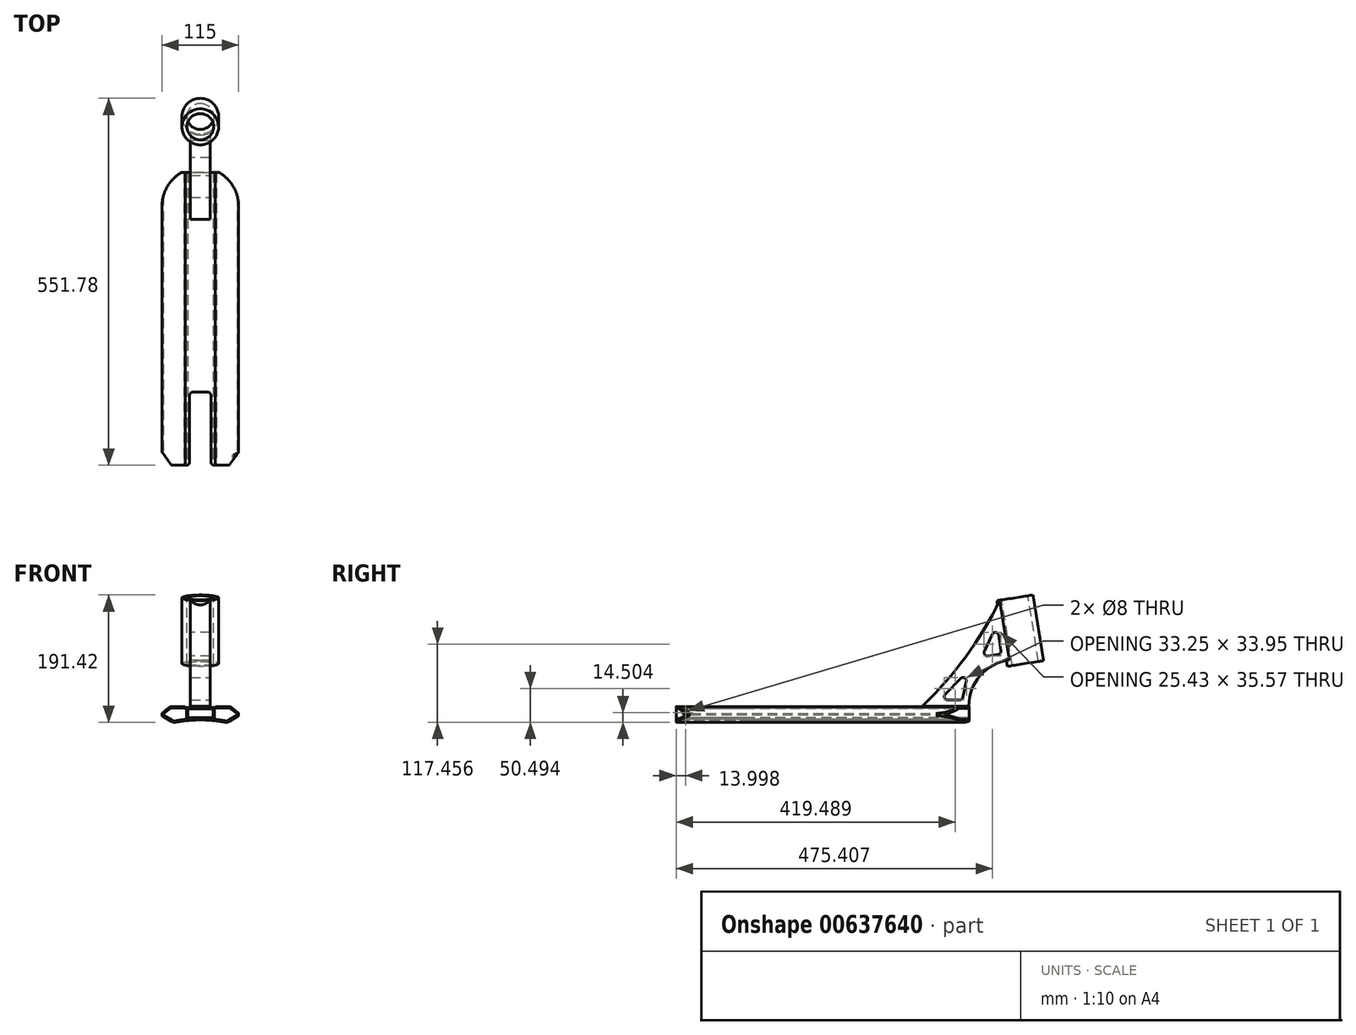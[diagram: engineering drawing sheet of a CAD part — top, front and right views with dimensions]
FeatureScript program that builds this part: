
annotation { "Feature Type Name" : "Feature", "Feature Type Description" : "" }
export const myFeature = defineFeature(function(context is Context, id is Id, definition is map)
    precondition{}
    {
        {
            var Q0;
            Q0=qCreatedBy(makeId("Front.planeOp"),FACE);
            var sketch = newSketch(context, id + "F0", { "sketchPlane" : qUnion([Q0])});
            skLineSegment(sketch, "E0", {"start": v(0, 0) * mm, "end": v(0, 46.3) * mm, "construction": true});
            skLineSegment(sketch, "E1", {"start": v(0, 23.15) * mm, "end": v(22.5, 23.15) * mm});
            skLineSegment(sketch, "E2", {"start": v(22.5, 23.15) * mm, "end": v(22.5, 24.45) * mm});
            skLineSegment(sketch, "E3", {"start": v(22.5, 24.45) * mm, "end": v(45.58, 24.45) * mm});
            skLineSegment(sketch, "E4", {"start": v(45.58, 24.45) * mm, "end": v(57.5, 14.45) * mm});
            skLineSegment(sketch, "E5", {"start": v(57.5, 14.45) * mm, "end": v(57.5, 10.45) * mm});
            skLineSegment(sketch, "E6", {"start": v(57.5, 10.45) * mm, "end": v(40.18, 0.45) * mm});
            skLineSegment(sketch, "E7.MirrorCS", {"start": v(0, 23.15) * mm, "end": v(-22.5, 23.15) * mm});
            skLineSegment(sketch, "E8.MirrorCS", {"start": v(-22.5, 24.45) * mm, "end": v(-45.58, 24.45) * mm});
            skLineSegment(sketch, "E9.MirrorCS", {"start": v(-45.58, 24.45) * mm, "end": v(-57.5, 14.45) * mm});
            skLineSegment(sketch, "E10.MirrorCS", {"start": v(-22.5, 23.15) * mm, "end": v(-22.5, 24.45) * mm});
            skLineSegment(sketch, "E11.MirrorCS", {"start": v(-57.5, 14.45) * mm, "end": v(-57.5, 10.45) * mm});
            skLineSegment(sketch, "E12.MirrorCS", {"start": v(-57.5, 10.45) * mm, "end": v(-40.18, 0.45) * mm});
            skArc(sketch, "E13", {"start": v(40.18, 0.45) * mm, "mid": v(0, 4.53) * mm, "end": v(-40.18, 0.45) * mm});
            skSolve(sketch);
        }
        {
            var Q0;
            Q0 = qSketchRegion(id + "F0", true);
            extrude(context, id + "F1", {"entities" : qUnion([Q0]), "endBound" : BoundingType.SYMMETRIC, "depth" : 500 * mm, "offsetDistance" : 25 * mm});
        }
        {
            var Q0;
            Q0=qCreatedBy(makeId("Front.planeOp"),FACE);
            var sketch = newSketch(context, id + "F2", { "sketchPlane" : qUnion([Q0])});
            skLineSegment(sketch, "E14.bottom", {"start": v(-19, 21.15) * mm, "end": v(19, 21.15) * mm});
            skLineSegment(sketch, "E14.top", {"start": v(-19, 8.15) * mm, "end": v(19, 8.15) * mm});
            skLineSegment(sketch, "E14.left", {"start": v(-19, 21.15) * mm, "end": v(-19, 8.15) * mm});
            skLineSegment(sketch, "E14.right", {"start": v(19, 21.15) * mm, "end": v(19, 8.15) * mm});
            skSolve(sketch);
        }
        {
            var Q0;
            Q0 = qSketchRegion(id + "F2", true);
            extrude(context, id + "F3", {"entities" : qUnion([Q0]), "operationType" : NewBodyOperationType.REMOVE, "endBound" : BoundingType.SYMMETRIC, "oppositeDirection" : true, "depth" : 500 * mm, "offsetDistance" : 25 * mm});
        }
        {
            var Q0;
            Q0=makeQuery(id+"F1.opExtrude","SWEPT_EDGE",EDGE,{"disambiguationData":[OSD([sQuery(id+"F0.wireOp",EDGE,"E8.MirrorCS"),sQuery(id+"F0.wireOp",EDGE,"E10.MirrorCS")])]});
            var Q1;
            Q1=makeQuery(id+"F1.opExtrude","SWEPT_EDGE",EDGE,{"disambiguationData":[OSD([sQuery(id+"F0.wireOp",EDGE,"E2"),sQuery(id+"F0.wireOp",EDGE,"E3")])]});
            fillet(context, id + "F4", {"entities" : qUnion([Q0, Q1]), "radius" : 2 * mm, "tangentPropagation" : true, "allowEdgeOverflow" : false});
        }
        {
            var Q0;
            Q0=makeQuery(id+"F1.opExtrude","SWEPT_EDGE",EDGE,{"disambiguationData":[OSD([sQuery(id+"F0.wireOp",EDGE,"E3"),sQuery(id+"F0.wireOp",EDGE,"E4")])]});
            var Q1;
            Q1=makeQuery(id+"F1.opExtrude","SWEPT_EDGE",EDGE,{"disambiguationData":[OSD([sQuery(id+"F0.wireOp",EDGE,"E6"),sQuery(id+"F0.wireOp",EDGE,"E13")])]});
            var Q2;
            Q2=makeQuery(id+"F1.opExtrude","SWEPT_EDGE",EDGE,{"disambiguationData":[OSD([sQuery(id+"F0.wireOp",EDGE,"E8.MirrorCS"),sQuery(id+"F0.wireOp",EDGE,"E9.MirrorCS")])]});
            var Q3;
            Q3=makeQuery(id+"F1.opExtrude","SWEPT_EDGE",EDGE,{"disambiguationData":[OSD([sQuery(id+"F0.wireOp",EDGE,"E12.MirrorCS"),sQuery(id+"F0.wireOp",EDGE,"E13")])]});
            fillet(context, id + "F5", {"entities" : qUnion([Q0, Q1, Q2, Q3]), "radius" : 9 * mm, "tangentPropagation" : true, "allowEdgeOverflow" : false});
        }
        {
            var Q0;
            Q0=makeQuery(id+"F1.opExtrude","SWEPT_EDGE",EDGE,{"disambiguationData":[OSD([sQuery(id+"F0.wireOp",EDGE,"E4"),sQuery(id+"F0.wireOp",EDGE,"E5")])]});
            var Q1;
            Q1=makeQuery(id+"F1.opExtrude","SWEPT_EDGE",EDGE,{"disambiguationData":[OSD([sQuery(id+"F0.wireOp",EDGE,"E5"),sQuery(id+"F0.wireOp",EDGE,"E6")])]});
            var Q2;
            Q2=makeQuery(id+"F1.opExtrude","SWEPT_EDGE",EDGE,{"disambiguationData":[OSD([sQuery(id+"F0.wireOp",EDGE,"E9.MirrorCS"),sQuery(id+"F0.wireOp",EDGE,"E11.MirrorCS")])]});
            var Q3;
            Q3=makeQuery(id+"F1.opExtrude","SWEPT_EDGE",EDGE,{"disambiguationData":[OSD([sQuery(id+"F0.wireOp",EDGE,"E11.MirrorCS"),sQuery(id+"F0.wireOp",EDGE,"E12.MirrorCS")])]});
            fillet(context, id + "F6", {"entities" : qUnion([Q0, Q1, Q2, Q3]), "radius" : 1 * mm, "tangentPropagation" : true, "allowEdgeOverflow" : false});
        }
        {
            var Q0;
            Q0=makeQuery(id+"F1.opExtrude","CAP_FACE",FACE,{"disambiguationData":[OSD([sQuery(id+"F0.wireOp",EDGE,"E1"),sQuery(id+"F0.wireOp",EDGE,"E2"),sQuery(id+"F0.wireOp",EDGE,"E3"),sQuery(id+"F0.wireOp",EDGE,"E4"),sQuery(id+"F0.wireOp",EDGE,"E5"),sQuery(id+"F0.wireOp",EDGE,"E6"),sQuery(id+"F0.wireOp",EDGE,"E7.MirrorCS"),sQuery(id+"F0.wireOp",EDGE,"E8.MirrorCS"),sQuery(id+"F0.wireOp",EDGE,"E9.MirrorCS"),sQuery(id+"F0.wireOp",EDGE,"E10.MirrorCS"),sQuery(id+"F0.wireOp",EDGE,"E11.MirrorCS"),sQuery(id+"F0.wireOp",EDGE,"E12.MirrorCS"),sQuery(id+"F0.wireOp",EDGE,"E13")])],"isStart":false});
            var sketch = newSketch(context, id + "F7", { "sketchPlane" : qUnion([Q0])});
            skLineSegment(sketch, "E15.0.0", {"start": v(-57.5, 13.98) * mm, "end": v(-57.5, 11.03) * mm});
            skArc(sketch, "E15.0.1", {"start": v(-57.5, 11.03) * mm, "mid": v(-57.37, 10.53) * mm, "end": v(-57, 10.16) * mm});
            skLineSegment(sketch, "E15.0.2", {"start": v(-57, 10.16) * mm, "end": v(-43.1, 2.14) * mm});
            skArc(sketch, "E15.0.3", {"start": v(-43.1, 2.14) * mm, "mid": v(-40.12, 1.06) * mm, "end": v(-36.94, 1.09) * mm});
            skArc(sketch, "E15.0.4", {"start": v(-36.94, 1.09) * mm, "mid": v(0, 4.53) * mm, "end": v(36.94, 1.09) * mm});
            skArc(sketch, "E15.0.5", {"start": v(36.94, 1.09) * mm, "mid": v(40.12, 1.06) * mm, "end": v(43.1, 2.14) * mm});
            skLineSegment(sketch, "E15.0.6", {"start": v(43.1, 2.14) * mm, "end": v(57, 10.16) * mm});
            skArc(sketch, "E15.0.7", {"start": v(57, 10.16) * mm, "mid": v(57.37, 10.53) * mm, "end": v(57.5, 11.03) * mm});
            skLineSegment(sketch, "E15.0.8", {"start": v(57.5, 11.03) * mm, "end": v(57.5, 13.98) * mm});
            skArc(sketch, "E15.0.9", {"start": v(57.5, 13.98) * mm, "mid": v(57.4, 14.4) * mm, "end": v(57.14, 14.75) * mm});
            skLineSegment(sketch, "E15.0.10", {"start": v(57.14, 14.75) * mm, "end": v(48.1, 22.35) * mm});
            skArc(sketch, "E15.0.11", {"start": v(48.1, 22.35) * mm, "mid": v(45.38, 23.9) * mm, "end": v(42.3, 24.45) * mm});
            skLineSegment(sketch, "E15.0.12", {"start": v(42.3, 24.45) * mm, "end": v(24.37, 24.45) * mm});
            skArc(sketch, "E15.0.13", {"start": v(24.37, 24.45) * mm, "mid": v(23.23, 24.1) * mm, "end": v(22.5, 23.15) * mm});
            skLineSegment(sketch, "E15.0.14", {"start": v(22.5, 23.15) * mm, "end": v(-22.5, 23.15) * mm});
            skArc(sketch, "E15.0.15", {"start": v(-22.5, 23.15) * mm, "mid": v(-23.23, 24.1) * mm, "end": v(-24.37, 24.45) * mm});
            skLineSegment(sketch, "E15.0.16", {"start": v(-24.37, 24.45) * mm, "end": v(-42.3, 24.45) * mm});
            skArc(sketch, "E15.0.17", {"start": v(-42.3, 24.45) * mm, "mid": v(-45.38, 23.9) * mm, "end": v(-48.1, 22.35) * mm});
            skLineSegment(sketch, "E15.0.18", {"start": v(-48.1, 22.35) * mm, "end": v(-57.14, 14.75) * mm});
            skArc(sketch, "E15.0.19", {"start": v(-57.14, 14.75) * mm, "mid": v(-57.4, 14.4) * mm, "end": v(-57.5, 13.98) * mm});
            skArc(sketch, "E16.0", {"start": v(-37.3, 3.05) * mm, "mid": v(0, 6.53) * mm, "end": v(37.3, 3.05) * mm});
            skArc(sketch, "E16.1", {"start": v(-42.1, 3.87) * mm, "mid": v(-39.78, 3.03) * mm, "end": v(-37.3, 3.05) * mm});
            skLineSegment(sketch, "E16.2", {"start": v(-55.5, 11.6) * mm, "end": v(-42.1, 3.87) * mm});
            skLineSegment(sketch, "E16.3", {"start": v(-55.5, 13.52) * mm, "end": v(-55.5, 11.6) * mm});
            skLineSegment(sketch, "E16.4", {"start": v(-24.37, 22.45) * mm, "end": v(-24.37, 22.45) * mm});
            skLineSegment(sketch, "E16.5", {"start": v(-24.37, 22.45) * mm, "end": v(-42.3, 22.45) * mm});
            skArc(sketch, "E16.6", {"start": v(-42.3, 22.45) * mm, "mid": v(-44.7, 22.03) * mm, "end": v(-46.8, 20.81) * mm});
            skLineSegment(sketch, "E16.7", {"start": v(-46.8, 20.81) * mm, "end": v(-55.5, 13.52) * mm});
            skArc(sketch, "E17", {"start": v(-22.73, 21.88) * mm, "mid": v(-23.48, 22.35) * mm, "end": v(-24.37, 22.45) * mm});
            skLineSegment(sketch, "E18", {"start": v(-22.73, 21.88) * mm, "end": v(-21, 21.88) * mm});
            skLineSegment(sketch, "E19", {"start": v(-21, 21.88) * mm, "end": v(-21, 5.43) * mm});
            skLineSegment(sketch, "E20.MirrorCS", {"start": v(21, 21.88) * mm, "end": v(21, 5.43) * mm});
            skLineSegment(sketch, "E21.MirrorCS", {"start": v(22.73, 21.88) * mm, "end": v(21, 21.88) * mm});
            skArc(sketch, "E22.MirrorCS", {"start": v(22.73, 21.88) * mm, "mid": v(23.48, 22.35) * mm, "end": v(24.37, 22.45) * mm});
            skLineSegment(sketch, "E23.MirrorCS", {"start": v(24.37, 22.45) * mm, "end": v(42.3, 22.45) * mm});
            skArc(sketch, "E24.MirrorCS", {"start": v(42.3, 22.45) * mm, "mid": v(44.7, 22.03) * mm, "end": v(46.8, 20.81) * mm});
            skLineSegment(sketch, "E25.MirrorCS", {"start": v(46.8, 20.81) * mm, "end": v(55.5, 13.52) * mm});
            skLineSegment(sketch, "E26.MirrorCS", {"start": v(55.5, 13.52) * mm, "end": v(55.5, 11.6) * mm});
            skLineSegment(sketch, "E27.MirrorCS", {"start": v(55.5, 11.6) * mm, "end": v(42.1, 3.87) * mm});
            skArc(sketch, "E28.MirrorCS", {"start": v(42.1, 3.87) * mm, "mid": v(39.78, 3.03) * mm, "end": v(37.3, 3.05) * mm});
            skArc(sketch, "E29.MirrorCS", {"start": v(37.3, 3.05) * mm, "mid": v(0, 6.53) * mm, "end": v(-37.3, 3.05) * mm});
            skSolve(sketch);
        }
        {
            var Q0;
            {var subQ0=sQuery(id+"F7.wireOp",EDGE,"E16.1");Q0=makeQuery(id+"F7.imprint","IMPRINT",FACE,{"disambiguationData":[TD([[makeQuery(id+"F7.imprint","IMPRINT",EDGE,{"derivedFrom":subQ0}),1.0]])]});}
            var Q1;
            Q1=makeQuery(id+"F7.imprint","IMPRINT",FACE,{"disambiguationData":[TD([[makeQuery(id+"F7.imprint","IMPRINT",EDGE,{"derivedFrom":sQuery(id+"F7.wireOp",EDGE,"E21.MirrorCS")}),1.0]])]});
            extrude(context, id + "F8", {"entities" : qUnion([Q0, Q1]), "operationType" : NewBodyOperationType.REMOVE, "endBound" : BoundingType.THROUGH_ALL, "oppositeDirection" : true, "depth" : 25 * mm, "offsetDistance" : 25 * mm});
        }
        {
            var Q0;
            Q0=qCreatedBy(makeId("Top.planeOp"),FACE);
            var sketch = newSketch(context, id + "F9", { "sketchPlane" : qUnion([Q0])});
            skArc(sketch, "E30", {"start": v(57.5, 199.99) * mm, "mid": v(0.07, 257.5) * mm, "end": v(-57.5, 200.13) * mm});
            skLineSegment(sketch, "E31.bottom", {"start": v(57.51, 199.99) * mm, "end": v(-57.5, 199.99) * mm});
            skLineSegment(sketch, "E31.top", {"start": v(57.51, 279.99) * mm, "end": v(-57.5, 279.99) * mm});
            skLineSegment(sketch, "E31.left", {"start": v(57.51, 199.99) * mm, "end": v(57.51, 279.99) * mm});
            skLineSegment(sketch, "E31.right", {"start": v(-57.5, 199.99) * mm, "end": v(-57.5, 279.99) * mm});
            skSolve(sketch);
        }
        {
            var Q0;
            {var subQ3=sQuery(id+"F9.wireOp",EDGE,"E30");Q0=makeQuery(id+"F9.imprint","IMPRINT",FACE,{"disambiguationData":[TD([[makeQuery(id+"F9.imprint","IMPRINT",EDGE,{"derivedFrom":subQ3}),-1.0]])]});}
            extrude(context, id + "F10", {"entities" : qUnion([Q0]), "operationType" : NewBodyOperationType.REMOVE, "endBound" : BoundingType.THROUGH_ALL, "depth" : 25 * mm, "offsetDistance" : 25 * mm});
        }
        {
            var Q0;
            {var subQ3=sQuery(id+"F9.wireOp",EDGE,"E30");Q0=makeQuery(id+"F9.imprint","IMPRINT",FACE,{"disambiguationData":[TD([[makeQuery(id+"F9.imprint","IMPRINT",EDGE,{"derivedFrom":subQ3}),-1.0]])]});}
            extrude(context, id + "F11", {"entities" : qUnion([Q0]), "operationType" : NewBodyOperationType.REMOVE, "endBound" : BoundingType.THROUGH_ALL, "oppositeDirection" : true, "depth" : 25 * mm, "offsetDistance" : 25 * mm, "hasSecondDirection" : true, "secondDirectionOppositeDirection" : false, "secondDirectionDepth" : 25 * mm});
        }
        {
            var Q0;
            Q0=qCreatedBy(makeId("Top.planeOp"),FACE);
            var sketch = newSketch(context, id + "F12", { "sketchPlane" : qUnion([Q0])});
            skLineSegment(sketch, "E32", {"start": v(-68, -156.01) * mm, "end": v(-68, -286.01) * mm});
            skLineSegment(sketch, "E33", {"start": v(-68, -286.01) * mm, "end": v(68, -286.01) * mm});
            skLineSegment(sketch, "E34", {"start": v(68, -286.01) * mm, "end": v(68, -156.01) * mm});
            skLineSegment(sketch, "E35", {"start": v(68, -156.01) * mm, "end": v(43.3, -190.01) * mm});
            skLineSegment(sketch, "E36", {"start": v(43.3, -190.01) * mm, "end": v(16, -190.01) * mm});
            skLineSegment(sketch, "E37", {"start": v(16, -190.01) * mm, "end": v(16, -80.01) * mm});
            skLineSegment(sketch, "E38", {"start": v(16, -80.01) * mm, "end": v(-16, -80.01) * mm});
            skLineSegment(sketch, "E39", {"start": v(-16, -80.01) * mm, "end": v(-16, -190.01) * mm});
            skLineSegment(sketch, "E40", {"start": v(-16, -190.01) * mm, "end": v(-43.3, -190.01) * mm});
            skLineSegment(sketch, "E41", {"start": v(-43.3, -190.01) * mm, "end": v(-68, -156.01) * mm});
            skSolve(sketch);
        }
        {
            var Q0;
            Q0 = qSketchRegion(id + "F12", true);
            extrude(context, id + "F13", {"entities" : qUnion([Q0]), "operationType" : NewBodyOperationType.REMOVE, "endBound" : BoundingType.THROUGH_ALL, "oppositeDirection" : true, "depth" : 25 * mm, "offsetDistance" : 25 * mm, "hasSecondDirection" : true, "secondDirectionBound" : SecondDirectionBoundingType.THROUGH_ALL, "secondDirectionOppositeDirection" : false, "secondDirectionDepth" : 25 * mm});
        }
        {
            var Q0;
            {var subQ0=sQuery(id+"F12.wireOp",EDGE,"E38");var subQ1=sQuery(id+"F12.wireOp",EDGE,"E39");Q0=makeQuery(id+"F13.boolean.opBoolean","COPY",EDGE,{"disambiguationData":[TD([makeQuery(id+"F3.boolean.opBoolean","COPY",FACE,{"derivedFrom":makeQuery(id+"F3.opExtrude","SWEPT_FACE",FACE,{"disambiguationData":[OSD([sQuery(id+"F2.wireOp",EDGE,"E14.bottom")])]})})])],"derivedFrom":makeQuery(id+"F13.opExtrude","SWEPT_EDGE",EDGE,{"disambiguationData":[OSD([subQ0,subQ1])]})});}
            var Q1;
            {var subQ0=sQuery(id+"F12.wireOp",EDGE,"E37");var subQ1=sQuery(id+"F12.wireOp",EDGE,"E38");Q1=makeQuery(id+"F13.boolean.opBoolean","COPY",EDGE,{"disambiguationData":[TD([makeQuery(id+"F3.boolean.opBoolean","COPY",FACE,{"derivedFrom":makeQuery(id+"F3.opExtrude","SWEPT_FACE",FACE,{"disambiguationData":[OSD([sQuery(id+"F2.wireOp",EDGE,"E14.bottom")])]})})])],"derivedFrom":makeQuery(id+"F13.opExtrude","SWEPT_EDGE",EDGE,{"disambiguationData":[OSD([subQ0,subQ1])]})});}
            var Q2;
            {var subQ0=sQuery(id+"F12.wireOp",EDGE,"E38");var subQ1=sQuery(id+"F12.wireOp",EDGE,"E37");Q2=makeQuery(id+"F13.boolean.opBoolean","COPY",EDGE,{"disambiguationData":[TD([makeQuery(id+"F1.opExtrude","SWEPT_FACE",FACE,{"disambiguationData":[OSD([sQuery(id+"F0.wireOp",EDGE,"E13")])]})])],"derivedFrom":makeQuery(id+"F13.opExtrude","SWEPT_EDGE",EDGE,{"disambiguationData":[OSD([subQ1,subQ0])]})});}
            var Q3;
            {var subQ0=sQuery(id+"F12.wireOp",EDGE,"E38");var subQ1=sQuery(id+"F12.wireOp",EDGE,"E39");Q3=makeQuery(id+"F13.boolean.opBoolean","COPY",EDGE,{"disambiguationData":[TD([makeQuery(id+"F1.opExtrude","SWEPT_FACE",FACE,{"disambiguationData":[OSD([sQuery(id+"F0.wireOp",EDGE,"E13")])]})])],"derivedFrom":makeQuery(id+"F13.opExtrude","SWEPT_EDGE",EDGE,{"disambiguationData":[OSD([subQ0,subQ1])]})});}
            var Q4;
            {var subQ0=sQuery(id+"F12.wireOp",EDGE,"E40");var subQ1=sQuery(id+"F12.wireOp",EDGE,"E39");Q4=makeQuery(id+"F13.boolean.opBoolean","COPY",EDGE,{"disambiguationData":[TD([makeQuery(id+"F3.boolean.opBoolean","COPY",FACE,{"derivedFrom":makeQuery(id+"F3.opExtrude","SWEPT_FACE",FACE,{"disambiguationData":[OSD([sQuery(id+"F2.wireOp",EDGE,"E14.bottom")])]})})])],"derivedFrom":makeQuery(id+"F13.opExtrude","SWEPT_EDGE",EDGE,{"disambiguationData":[OSD([subQ1,subQ0])]})});}
            var Q5;
            {var subQ0=sQuery(id+"F12.wireOp",EDGE,"E37");var subQ1=sQuery(id+"F12.wireOp",EDGE,"E36");Q5=makeQuery(id+"F13.boolean.opBoolean","COPY",EDGE,{"disambiguationData":[TD([makeQuery(id+"F3.boolean.opBoolean","COPY",FACE,{"derivedFrom":makeQuery(id+"F3.opExtrude","SWEPT_FACE",FACE,{"disambiguationData":[OSD([sQuery(id+"F2.wireOp",EDGE,"E14.bottom")])]})})])],"derivedFrom":makeQuery(id+"F13.opExtrude","SWEPT_EDGE",EDGE,{"disambiguationData":[OSD([subQ1,subQ0])]})});}
            var Q6;
            {var subQ0=sQuery(id+"F12.wireOp",EDGE,"E39");var subQ1=sQuery(id+"F12.wireOp",EDGE,"E40");Q6=makeQuery(id+"F13.boolean.opBoolean","COPY",EDGE,{"disambiguationData":[TD([makeQuery(id+"F1.opExtrude","SWEPT_FACE",FACE,{"disambiguationData":[OSD([sQuery(id+"F0.wireOp",EDGE,"E13")])]})])],"derivedFrom":makeQuery(id+"F13.opExtrude","SWEPT_EDGE",EDGE,{"disambiguationData":[OSD([subQ0,subQ1])]})});}
            var Q7;
            {var subQ0=sQuery(id+"F12.wireOp",EDGE,"E36");var subQ1=sQuery(id+"F12.wireOp",EDGE,"E37");Q7=makeQuery(id+"F13.boolean.opBoolean","COPY",EDGE,{"disambiguationData":[TD([makeQuery(id+"F1.opExtrude","SWEPT_FACE",FACE,{"disambiguationData":[OSD([sQuery(id+"F0.wireOp",EDGE,"E13")])]})])],"derivedFrom":makeQuery(id+"F13.opExtrude","SWEPT_EDGE",EDGE,{"disambiguationData":[OSD([subQ0,subQ1])]})});}
            fillet(context, id + "F14", {"entities" : qUnion([Q0, Q1, Q2, Q3, Q4, Q5, Q6, Q7]), "radius" : 5 * mm, "tangentPropagation" : true, "allowEdgeOverflow" : false});
        }
        {
            var Q0;
            Q0=qCreatedBy(makeId("Right.planeOp"),FACE);
            var sketch = newSketch(context, id + "F15", { "sketchPlane" : qUnion([Q0])});
            skLineSegment(sketch, "E42", {"start": v(249.7, 25.24) * mm, "end": v(179.7, 25.24) * mm});
            skArc(sketch, "E43", {"start": v(179.7, 25.24) * mm, "mid": v(245.17, 99.57) * mm, "end": v(296.25, 184.45) * mm});
            skLineSegment(sketch, "E44", {"start": v(296.25, 184.45) * mm, "end": v(341.68, 191.65) * mm});
            skLineSegment(sketch, "E45", {"start": v(341.68, 191.65) * mm, "end": v(357.32, 92.88) * mm});
            skLineSegment(sketch, "E46", {"start": v(357.32, 92.88) * mm, "end": v(311.9, 85.68) * mm});
            skLineSegment(sketch, "E47", {"start": v(311.9, 85.68) * mm, "end": v(310.47, 94.63) * mm});
            skArc(sketch, "E48", {"start": v(310.47, 94.63) * mm, "mid": v(267.04, 71.36) * mm, "end": v(249.7, 25.24) * mm});
            skSolve(sketch);
        }
        {
            var Q0;
            Q0=makeQuery(id+"F15.imprint","IMPRINT",FACE,{"disambiguationData":[TD([[makeQuery(id+"F15.imprint","IMPRINT",EDGE,{"derivedFrom":sQuery(id+"F15.wireOp",EDGE,"E42")}),-1.0]])]});
            extrude(context, id + "F16", {"entities" : qUnion([Q0]), "operationType" : NewBodyOperationType.ADD, "endBound" : BoundingType.SYMMETRIC, "depth" : 30 * mm, "offsetDistance" : 25 * mm});
        }
        {
            var Q0;
            Q0=makeQuery(id+"F16.opExtrude","SWEPT_FACE",FACE,{"disambiguationData":[OSD([sQuery(id+"F15.wireOp",EDGE,"E44")])]});
            var sketch = newSketch(context, id + "F17", { "sketchPlane" : qUnion([Q0])});
            skCircle(sketch, "E49", {"center": v(0, 344.45) * mm, "radius": 27.5 * mm});
            skSolve(sketch);
        }
        {
            var Q0;
            Q0=makeQuery(id+"F17.imprint","IMPRINT",FACE,{"disambiguationData":[TD([[makeQuery(id+"F17.imprint","IMPRINT",EDGE,{"derivedFrom":sQuery(id+"F17.wireOp",EDGE,"E49")}),1.0]])]});
            var Q1;
            Q1=makeQuery(id+"F16.opExtrude","SWEPT_FACE",FACE,{"disambiguationData":[OSD([sQuery(id+"F15.wireOp",EDGE,"E46")])]});
            extrude(context, id + "F18", {"entities" : qUnion([Q0]), "operationType" : NewBodyOperationType.ADD, "endBound" : BoundingType.UP_TO_SURFACE, "oppositeDirection" : true, "depth" : 25 * mm, "endBoundEntityFace" : qUnion([Q1]), "offsetDistance" : 25 * mm});
        }
        {
            var Q0;
            {var subQ0=sQuery(id+"F15.wireOp",EDGE,"E44");Q0=makeQuery(id+"F18.boolean.opBoolean","MERGE",FACE,{"derivedFrom":[makeQuery(id+"F16.opExtrude","SWEPT_FACE",FACE,{"disambiguationData":[OSD([subQ0])]}),makeQuery(id+"F18.opExtrude","CAP_FACE",FACE,{"disambiguationData":[OSD([sQuery(id+"F15.wireOp",EDGE,"E43"),subQ0,sQuery(id+"F15.wireOp",EDGE,"E45"),sQuery(id+"F17.wireOp",EDGE,"E49")])],"isStart":true})]});}
            var sketch = newSketch(context, id + "F19", { "sketchPlane" : qUnion([Q0])});
            skPoint(sketch, "E50", {"position": v(0, 344.45) * mm});
            skSolve(sketch);
        }
        {
            var Q0;
            Q0=sQuery(id+"F19.wireOp",VERTEX,"E50");
            var Q1;
            Q1=makeQuery(id+"F16.opExtrude","SWEPT_BODY",BODY,{"disambiguationData":[OSD([sQuery(id+"F15.wireOp",EDGE,"E42"),sQuery(id+"F15.wireOp",EDGE,"E43"),sQuery(id+"F15.wireOp",EDGE,"E44"),sQuery(id+"F15.wireOp",EDGE,"E45"),sQuery(id+"F15.wireOp",EDGE,"E46"),sQuery(id+"F15.wireOp",EDGE,"E47"),sQuery(id+"F15.wireOp",EDGE,"E48")])]});
            hole(context, id + "F20", {"style" : HoleStyle.SIMPLE, "endStyle" : HoleEndStyle.THROUGH, "holeDiameter" : 40 * mm, "majorDiameter" : 5 * mm, "isTappedThrough" : true, "tappedDepth" : 12 * mm, "tapClearance" : 3, "locations" : qUnion([Q0]), "scope" : qUnion([Q1])});
        }
        {
            var Q0;
            Q0=makeQuery(id+"F8.boolean.opBoolean","COPY",FACE,{"derivedFrom":makeQuery(id+"F8.opExtrude","SWEPT_FACE",FACE,{"disambiguationData":[OSD([sQuery(id+"F7.wireOp",EDGE,"E19")])]})});
            var sketch = newSketch(context, id + "F21", { "sketchPlane" : qUnion([Q0])});
            skPoint(sketch, "E51", {"position": v(176.01, 15.43) * mm});
            skSolve(sketch);
        }
        {
            var Q0;
            Q0=sQuery(id+"F21.wireOp",VERTEX,"E51");
            var Q1;
            Q1=makeQuery(id+"F1.opExtrude","SWEPT_BODY",BODY,{"disambiguationData":[OSD([sQuery(id+"F0.wireOp",EDGE,"E1"),sQuery(id+"F0.wireOp",EDGE,"E2"),sQuery(id+"F0.wireOp",EDGE,"E3"),sQuery(id+"F0.wireOp",EDGE,"E4"),sQuery(id+"F0.wireOp",EDGE,"E5"),sQuery(id+"F0.wireOp",EDGE,"E6"),sQuery(id+"F0.wireOp",EDGE,"E7.MirrorCS"),sQuery(id+"F0.wireOp",EDGE,"E8.MirrorCS"),sQuery(id+"F0.wireOp",EDGE,"E9.MirrorCS"),sQuery(id+"F0.wireOp",EDGE,"E10.MirrorCS"),sQuery(id+"F0.wireOp",EDGE,"E11.MirrorCS"),sQuery(id+"F0.wireOp",EDGE,"E12.MirrorCS"),sQuery(id+"F0.wireOp",EDGE,"E13")])]});
            hole(context, id + "F22", {"style" : HoleStyle.SIMPLE, "endStyle" : HoleEndStyle.THROUGH, "holeDiameter" : 8 * mm, "majorDiameter" : 5 * mm, "isTappedThrough" : true, "tappedDepth" : 12 * mm, "tapClearance" : 3, "locations" : qUnion([Q0]), "scope" : qUnion([Q1])});
        }
        {
            var Q0;
            Q0=makeQuery(id+"F16.opExtrude","CAP_FACE",FACE,{"disambiguationData":[OSD([sQuery(id+"F15.wireOp",EDGE,"E42"),sQuery(id+"F15.wireOp",EDGE,"E43"),sQuery(id+"F15.wireOp",EDGE,"E44"),sQuery(id+"F15.wireOp",EDGE,"E45"),sQuery(id+"F15.wireOp",EDGE,"E46"),sQuery(id+"F15.wireOp",EDGE,"E47"),sQuery(id+"F15.wireOp",EDGE,"E48")])],"isStart":false});
            var sketch = newSketch(context, id + "F23", { "sketchPlane" : qUnion([Q0])});
            skLineSegment(sketch, "E52", {"start": v(206, 34.45) * mm, "end": v(240, 34.45) * mm});
            skLineSegment(sketch, "E53", {"start": v(240, 34.45) * mm, "end": v(249.7, 79.45) * mm});
            skLineSegment(sketch, "E54", {"start": v(206, 34.45) * mm, "end": v(249.7, 79.45) * mm});
            skLineSegment(sketch, "E55", {"start": v(291.8, 148.3) * mm, "end": v(298.84, 103.86) * mm});
            skLineSegment(sketch, "E56", {"start": v(298.84, 103.86) * mm, "end": v(269.2, 99.17) * mm});
            skLineSegment(sketch, "E57", {"start": v(269.2, 99.17) * mm, "end": v(291.8, 148.3) * mm});
            skSolve(sketch);
        }
        {
            var Q0;
            Q0=makeQuery(id+"F23.imprint","IMPRINT",FACE,{"disambiguationData":[TD([[makeQuery(id+"F23.imprint","IMPRINT",EDGE,{"derivedFrom":sQuery(id+"F23.wireOp",EDGE,"E55")}),-1.0]])]});
            var Q1;
            Q1=makeQuery(id+"F23.imprint","IMPRINT",FACE,{"disambiguationData":[TD([[makeQuery(id+"F23.imprint","IMPRINT",EDGE,{"derivedFrom":sQuery(id+"F23.wireOp",EDGE,"E52")}),1.0]])]});
            extrude(context, id + "F24", {"entities" : qUnion([Q0, Q1]), "operationType" : NewBodyOperationType.REMOVE, "endBound" : BoundingType.THROUGH_ALL, "oppositeDirection" : true, "depth" : 25 * mm, "offsetDistance" : 25 * mm});
        }
        {
            var Q0;
            Q0=makeQuery(id+"F24.boolean.opBoolean","COPY",EDGE,{"derivedFrom":makeQuery(id+"F24.opExtrude","SWEPT_EDGE",EDGE,{"disambiguationData":[OSD([sQuery(id+"F23.wireOp",EDGE,"E55"),sQuery(id+"F23.wireOp",EDGE,"E57")])]})});
            var Q1;
            Q1=makeQuery(id+"F24.boolean.opBoolean","COPY",EDGE,{"derivedFrom":makeQuery(id+"F24.opExtrude","SWEPT_EDGE",EDGE,{"disambiguationData":[OSD([sQuery(id+"F23.wireOp",EDGE,"E55"),sQuery(id+"F23.wireOp",EDGE,"E56")])]})});
            var Q2;
            Q2=makeQuery(id+"F24.boolean.opBoolean","COPY",EDGE,{"derivedFrom":makeQuery(id+"F24.opExtrude","SWEPT_EDGE",EDGE,{"disambiguationData":[OSD([sQuery(id+"F23.wireOp",EDGE,"E56"),sQuery(id+"F23.wireOp",EDGE,"E57")])]})});
            var Q3;
            Q3=makeQuery(id+"F24.boolean.opBoolean","COPY",EDGE,{"derivedFrom":makeQuery(id+"F24.opExtrude","SWEPT_EDGE",EDGE,{"disambiguationData":[OSD([sQuery(id+"F23.wireOp",EDGE,"E53"),sQuery(id+"F23.wireOp",EDGE,"E54")])]})});
            var Q4;
            Q4=makeQuery(id+"F24.boolean.opBoolean","COPY",EDGE,{"derivedFrom":makeQuery(id+"F24.opExtrude","SWEPT_EDGE",EDGE,{"disambiguationData":[OSD([sQuery(id+"F23.wireOp",EDGE,"E52"),sQuery(id+"F23.wireOp",EDGE,"E53")])]})});
            var Q5;
            Q5=makeQuery(id+"F24.boolean.opBoolean","COPY",EDGE,{"derivedFrom":makeQuery(id+"F24.opExtrude","SWEPT_EDGE",EDGE,{"disambiguationData":[OSD([sQuery(id+"F23.wireOp",EDGE,"E52"),sQuery(id+"F23.wireOp",EDGE,"E54")])]})});
            fillet(context, id + "F25", {"entities" : qUnion([Q0, Q1, Q2, Q3, Q4, Q5]), "radius" : 5 * mm, "tangentPropagation" : true, "allowEdgeOverflow" : false});
        }
    });
